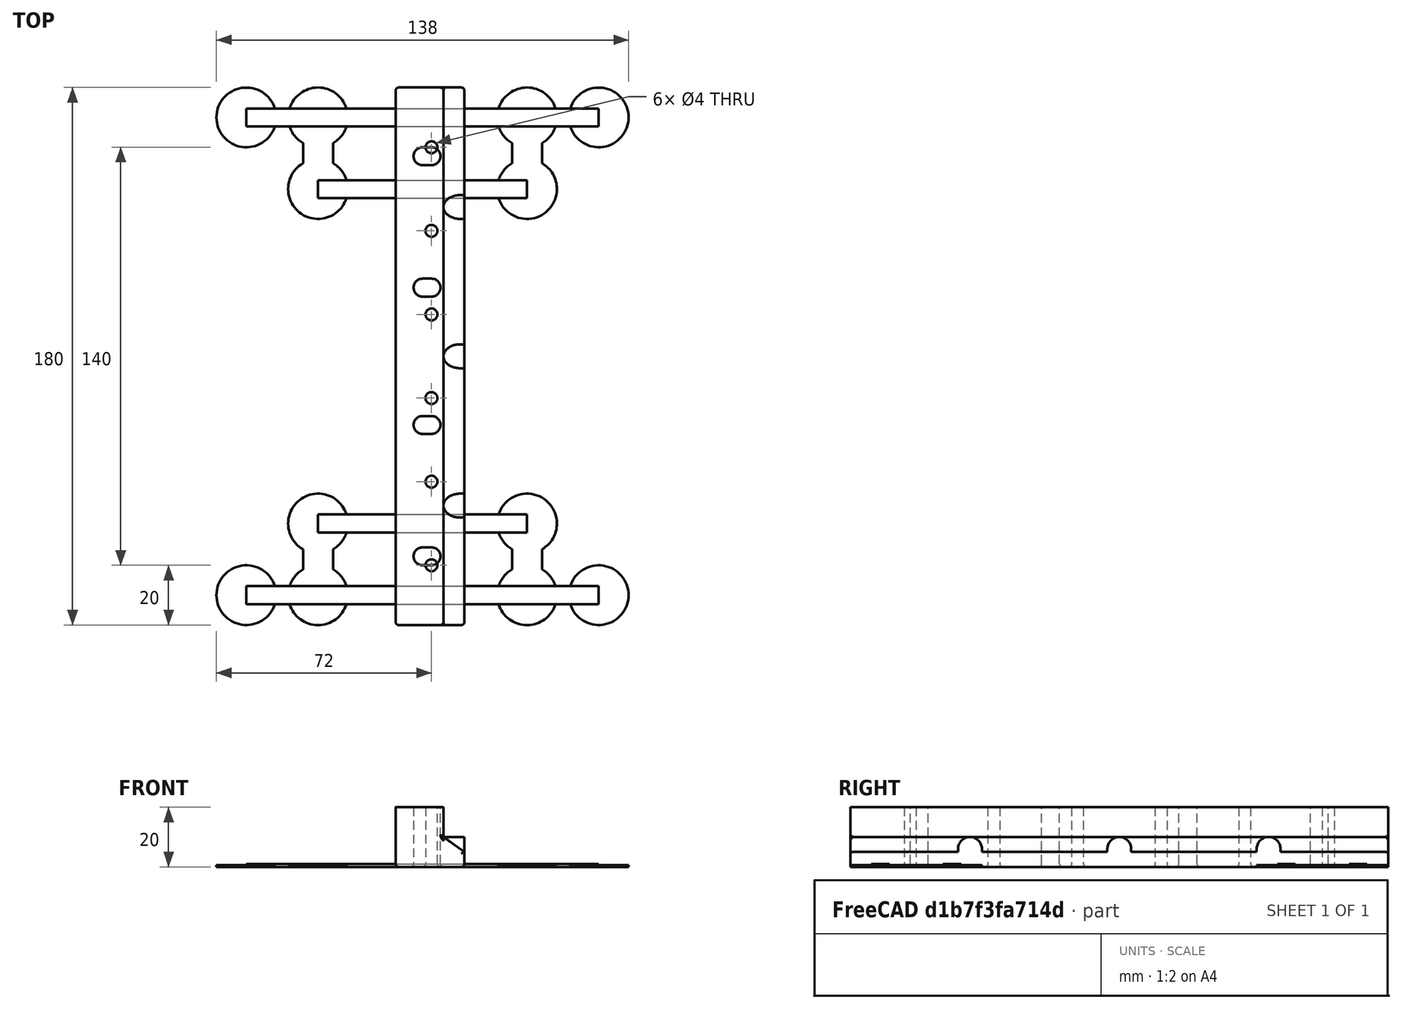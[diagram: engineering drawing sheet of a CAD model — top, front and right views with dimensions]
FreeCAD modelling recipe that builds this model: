
FCSTD DOCUMENT  (FreeCAD 0.21R33771 (Git))
Label: Battery_Bracket
License: All rights reserved
LicenseURL: https://en.wikipedia.org/wiki/All_rights_reserved
objects: Part::Cylinder×32, Part::Box×22, Part::MultiFuse×13, Part::Cut×10, App::Part×3, Part::Chamfer×2, Part::Fillet×2
note: 81 computed .brp shape members not serialized (recipe doc carries the construction recipe); baked Part::Feature solids carry a one-line shape summary decoded from their .brp

FEATURE [Part::Box] Box  label="Cube"
  AttacherType = Attacher::AttachEngine3D
  Height = 10
  Length = 23
  Placement = pos=(-4,0,5) rot=(0,0,1;0rad)
  Width = 180
FEATURE [Part::Cylinder] Cylinder
  Angle = 180
  AttacherType = Attacher::AttachEngine3D
  FirstAngle = 0
  Height = 7
  Placement = pos=(12,90,11) rot=(0.57735,0.57735,0.57735;2.0944rad)
  Radius = 4
  SecondAngle = 0
FEATURE [Part::Cylinder] Cylinder001
  Angle = 180
  AttacherType = Attacher::AttachEngine3D
  FirstAngle = 0
  Height = 7
  Placement = pos=(12,140,11) rot=(0.57735,0.57735,0.57735;2.0944rad)
  Radius = 4
  SecondAngle = 0
FEATURE [Part::Cylinder] Cylinder002
  Angle = 180
  AttacherType = Attacher::AttachEngine3D
  FirstAngle = 0
  Height = 7
  Placement = pos=(12,40,11) rot=(0.57735,0.57735,0.57735;2.0944rad)
  Radius = 4
  SecondAngle = 0
FEATURE [Part::Box] Box001  label="Cube001"
  AttacherType = Attacher::AttachEngine3D
  Height = 1
  Length = 7
  Placement = pos=(12,86,10) rot=(0,0,1;0rad)
  Width = 8
FEATURE [Part::Box] Box002  label="Cube002"
  AttacherType = Attacher::AttachEngine3D
  Height = 1
  Length = 7
  Placement = pos=(12,136,10) rot=(0,0,1;0rad)
  Width = 8
FEATURE [Part::Box] Box003  label="Cube003"
  AttacherType = Attacher::AttachEngine3D
  Height = 1
  Length = 7
  Placement = pos=(12,36,10) rot=(0,0,1;0rad)
  Width = 8
FEATURE [Part::MultiFuse] Fusion  label="Fusion000"
  Shapes = -> [Box002,Cylinder001]
FEATURE [Part::MultiFuse] Fusion001
  Shapes = -> [Cylinder,Box001]
FEATURE [Part::MultiFuse] Fusion002
  Shapes = -> [Cylinder002,Box003]
FEATURE [Part::Cylinder] Cylinder003
  Angle = 360
  AttacherType = Attacher::AttachEngine3D
  FirstAngle = 0
  Height = 20
  Placement = pos=(8,23,5) rot=(0,0,1;0rad)
  Radius = 3
  SecondAngle = 0
FEATURE [Part::Cylinder] Cylinder004
  Angle = 360
  AttacherType = Attacher::AttachEngine3D
  FirstAngle = 0
  Height = 20
  Placement = pos=(8,157,5) rot=(0,0,1;0rad)
  Radius = 3
  SecondAngle = 0
FEATURE [Part::Chamfer] Chamfer
  Base = -> Box
  Edges = 1 edges: [Edge6 r1=5 r2=7]
FEATURE [Part::Box] Box005  label="Cube005"
  AttacherType = Attacher::AttachEngine3D
  Height = 10
  Length = 16
  Placement = pos=(-4,0,15) rot=(0,0,1;0rad)
  Width = 180
FEATURE [Part::Box] Box008  label="Cube008"
  AttacherType = Attacher::AttachEngine3D
  Height = 10
  Length = 23
  Placement = pos=(-4,0,5) rot=(0,0,1;0rad)
  Width = 180
FEATURE [Part::Box] Box009  label="Cube009"
  AttacherType = Attacher::AttachEngine3D
  Height = 1
  Length = 7
  Placement = pos=(12,86,10) rot=(0,0,1;0rad)
  Width = 8
FEATURE [Part::Box] Box010  label="Cube010"
  AttacherType = Attacher::AttachEngine3D
  Height = 1
  Length = 7
  Placement = pos=(12,136,10) rot=(0,0,1;0rad)
  Width = 8
FEATURE [Part::Box] Box011  label="Cube011"
  AttacherType = Attacher::AttachEngine3D
  Height = 1
  Length = 7
  Placement = pos=(12,36,10) rot=(0,0,1;0rad)
  Width = 8
FEATURE [Part::Box] Box012  label="Cube012"
  AttacherType = Attacher::AttachEngine3D
  Height = 10
  Length = 16
  Placement = pos=(-4,0,15) rot=(0,0,1;0rad)
  Width = 180
FEATURE [Part::Chamfer] Chamfer001
  Base = -> Box008
  Edges = 1 edges: [Edge6 r1=5 r2=7]
FEATURE [Part::Cylinder] Cylinder005
  Angle = 180
  AttacherType = Attacher::AttachEngine3D
  FirstAngle = 0
  Height = 7
  Placement = pos=(12,90,11) rot=(0.57735,0.57735,0.57735;2.0944rad)
  Radius = 4
  SecondAngle = 0
FEATURE [Part::Cylinder] Cylinder006
  Angle = 180
  AttacherType = Attacher::AttachEngine3D
  FirstAngle = 0
  Height = 7
  Placement = pos=(12,140,11) rot=(0.57735,0.57735,0.57735;2.0944rad)
  Radius = 4
  SecondAngle = 0
FEATURE [Part::Cylinder] Cylinder007
  Angle = 180
  AttacherType = Attacher::AttachEngine3D
  FirstAngle = 0
  Height = 7
  Placement = pos=(12,40,11) rot=(0.57735,0.57735,0.57735;2.0944rad)
  Radius = 4
  SecondAngle = 0
FEATURE [Part::Cylinder] Cylinder009
  Angle = 360
  AttacherType = Attacher::AttachEngine3D
  FirstAngle = 0
  Height = 20
  Placement = pos=(8,160,5) rot=(0,0,1;0rad)
  Radius = 2
  SecondAngle = 0
FEATURE [Part::MultiFuse] Fusion004
  Shapes = -> [Box010,Cylinder006]
FEATURE [Part::MultiFuse] Fusion005
  Shapes = -> [Cylinder005,Box009]
FEATURE [Part::MultiFuse] Fusion006
  Shapes = -> [Cylinder007,Box011]
FEATURE [Part::Cylinder] Cylinder010 .. Cylinder014  x5 (patterned run collapsed; names and placements below)
  Angle = 360
  AttacherType = Attacher::AttachEngine3D
  FirstAngle = 0
  Height = 20
  Radius = 2
  SecondAngle = 0
  placements: 5 in arithmetic series — first pos=(8,132,5) rot=(0,0,1;0rad), step (0,-28,0), last pos=(8,20,5) rot=(0,0,1;0rad)
FEATURE [Part::MultiFuse] Fusion009
  Shapes = -> [Chamfer001,Box012,Fusion006,Fusion005,Fusion004]
FEATURE [Part::Cylinder] Cylinder015
  Angle = 360
  AttacherType = Attacher::AttachEngine3D
  FirstAngle = 0
  Height = 20
  Placement = pos=(5,157,5) rot=(0,0,1;0rad)
  Radius = 3
  SecondAngle = 0
FEATURE [Part::Cylinder] Cylinder016
  Angle = 360
  AttacherType = Attacher::AttachEngine3D
  FirstAngle = 0
  Height = 20
  Placement = pos=(5,23,5) rot=(0,0,1;0rad)
  Radius = 3
  SecondAngle = 0
FEATURE [Part::Box] Box013  label="Cube013"
  AttacherType = Attacher::AttachEngine3D
  Height = 20
  Length = 3
  Placement = pos=(5,20,5) rot=(0,0,1;0rad)
  Width = 6
FEATURE [Part::Box] Box014  label="Cube014"
  AttacherType = Attacher::AttachEngine3D
  Height = 20
  Length = 3
  Placement = pos=(5,154,5) rot=(0,0,1;0rad)
  Width = 6
FEATURE [Part::MultiFuse] Fusion010
  Shapes = -> [Box014,Cylinder015,Cylinder004]
FEATURE [Part::MultiFuse] Fusion011
  Shapes = -> [Cylinder003,Cylinder016,Box013]
FEATURE [Part::Cylinder] Cylinder017
  Angle = 360
  AttacherType = Attacher::AttachEngine3D
  FirstAngle = 0
  Height = 0.6
  Placement = pos=(-54,10,5) rot=(0,0,1;0rad)
  Radius = 10
  SecondAngle = 0
FEATURE [Part::Cylinder] Cylinder018
  Angle = 360
  AttacherType = Attacher::AttachEngine3D
  FirstAngle = 0
  Height = 0.6
  Placement = pos=(64,10,5) rot=(0,0,1;0rad)
  Radius = 10
  SecondAngle = 0
FEATURE [Part::Cylinder] Cylinder019
  Angle = 360
  AttacherType = Attacher::AttachEngine3D
  FirstAngle = 0
  Height = 0.6
  Placement = pos=(-54,170,5) rot=(0,0,1;0rad)
  Radius = 10
  SecondAngle = 0
FEATURE [Part::Cylinder] Cylinder020
  Angle = 360
  AttacherType = Attacher::AttachEngine3D
  FirstAngle = 0
  Height = 0.6
  Placement = pos=(40,146,5) rot=(0,0,1;0rad)
  Radius = 10
  SecondAngle = 0
FEATURE [Part::Box] Box015  label="Cube015"
  AttacherType = Attacher::AttachEngine3D
  Height = 1
  Length = 70
  Placement = pos=(-30,31,5) rot=(0,0,1;0rad)
  Width = 6
FEATURE [Part::Box] Box016  label="Cube016"
  AttacherType = Attacher::AttachEngine3D
  Height = 1
  Length = 70
  Placement = pos=(-30,143,5) rot=(0,0,1;0rad)
  Width = 6
FEATURE [Part::Box] Box017  label="Cube017"
  AttacherType = Attacher::AttachEngine3D
  Height = 20
  Length = 3
  Placement = pos=(5,20,5) rot=(0,0,1;0rad)
  Width = 6
FEATURE [Part::Cylinder] Cylinder021
  Angle = 360
  AttacherType = Attacher::AttachEngine3D
  FirstAngle = 0
  Height = 20
  Placement = pos=(8,23,5) rot=(0,0,1;0rad)
  Radius = 3
  SecondAngle = 0
FEATURE [Part::Cylinder] Cylinder022
  Angle = 360
  AttacherType = Attacher::AttachEngine3D
  FirstAngle = 0
  Height = 20
  Placement = pos=(5,23,5) rot=(0,0,1;0rad)
  Radius = 3
  SecondAngle = 0
FEATURE [Part::MultiFuse] Fusion013
  Placement = pos=(0,90,0) rot=(0,0,1;0rad)
  Shapes = -> [Cylinder021,Cylinder022,Box017]
FEATURE [Part::Box] Box018  label="Cube018"
  AttacherType = Attacher::AttachEngine3D
  Height = 20
  Length = 3
  Placement = pos=(5,20,5) rot=(0,0,1;0rad)
  Width = 6
FEATURE [Part::Cylinder] Cylinder023
  Angle = 360
  AttacherType = Attacher::AttachEngine3D
  FirstAngle = 0
  Height = 20
  Placement = pos=(8,23,5) rot=(0,0,1;0rad)
  Radius = 3
  SecondAngle = 0
FEATURE [Part::Cylinder] Cylinder024
  Angle = 360
  AttacherType = Attacher::AttachEngine3D
  FirstAngle = 0
  Height = 20
  Placement = pos=(5,23,5) rot=(0,0,1;0rad)
  Radius = 3
  SecondAngle = 0
FEATURE [Part::MultiFuse] Fusion014
  Placement = pos=(0,44,0) rot=(0,0,1;0rad)
  Shapes = -> [Cylinder023,Cylinder024,Box018]
FEATURE [Part::MultiFuse] Fusion016
  Shapes = -> [Box005,Fusion001,Fusion002,Fusion,Chamfer]
FEATURE [Part::Cut] Cut006
  Base = -> Fusion016
  Tool = -> Fusion010
FEATURE [Part::Cut] Cut007
  Base = -> Cut006
  Tool = -> Fusion014
FEATURE [Part::Cut] Cut008
  Base = -> Cut007
  Tool = -> Fusion013
FEATURE [Part::Cut] Cut009
  Base = -> Cut008
  Tool = -> Fusion011
FEATURE [Part::Fillet] Fillet001
  Base = -> Cut009
  Edges = 34 edges r=1: [Edge1,Edge3,Edge6,Edge31,Edge32,Edge33,Edge34,Edge35,Edge36,Edge37,Edge42,Edge45,Edge47,Edge49,Edge51,Edge52,Edge56,Edge57,Edge59,Edge61,Edge62,Edge66,Edge67,Edge69,Edge71,Edge72,Edge76,Edge77,Edge79,Edge81,Edge82,Edge83,Edge84,Edge85]
FEATURE [App::Part] Part  label="Front"
  Group = -> [Cut007,Cut008,Fusion016,Cut006,Box,Fusion001,Fusion002,Cylinder,Cylinder001,Cylinder002,Box001,Box002,Box003,Fusion,Cylinder003,Cylinder004,Chamfer,Box005,Cylinder015,Cylinder016,Box013,Box014,Fusion010,Fusion011,Box017,Cylinder021,Cylinder022,Fusion013,Box018,Cylinder023,Cylinder024,Fusion014,Cut009,Fillet001]
  Origin = -> Origin
  Placement = pos=(0,180,0) rot=(0,0,1;3.14159rad)
FEATURE [Part::Cut] Cut
  Base = -> Fusion009
  Tool = -> Cylinder009
FEATURE [Part::Cut] Cut010
  Base = -> Cut
  Tool = -> Cylinder010
FEATURE [Part::Cut] Cut011
  Base = -> Cut010
  Tool = -> Cylinder011
FEATURE [Part::Cut] Cut012
  Base = -> Cut011
  Tool = -> Cylinder012
FEATURE [Part::Cut] Cut013
  Base = -> Cut012
  Tool = -> Cylinder013
FEATURE [Part::Cut] Cut014
  Base = -> Cut013
  Tool = -> Cylinder014
FEATURE [Part::Fillet] Fillet
  Base = -> Cut014
  Edges = 20 edges r=1: [Edge1,Edge3,Edge6,Edge17,Edge18,Edge19,Edge20,Edge21,Edge22,Edge23,Edge29,Edge31,Edge33,Edge35,Edge37,Edge39,Edge40,Edge41,Edge42,Edge43]
FEATURE [App::Part] Part001  label="Rear"
  Group = -> [Cut013,Cut011,Cut010,Cut012,Box008,Box009,Box010,Box011,Box012,Chamfer001,Cylinder005,Cylinder006,Cylinder007,Cylinder009,Fusion004,Fusion005,Fusion006,Cylinder010,Cylinder011,Cylinder012,Cylinder013,Cylinder014,Fusion009,Cut,Cut014,Fillet]
  Origin = -> Origin001
  Placement = pos=(10,0,0) rot=(0,0,1;0rad)
FEATURE [Part::Cylinder] Cylinder025
  Angle = 360
  AttacherType = Attacher::AttachEngine3D
  FirstAngle = 0
  Height = 0.6
  Placement = pos=(40,34,5) rot=(0,0,1;0rad)
  Radius = 10
  SecondAngle = 0
FEATURE [Part::Cylinder] Cylinder026
  Angle = 360
  AttacherType = Attacher::AttachEngine3D
  FirstAngle = 0
  Height = 0.6
  Placement = pos=(-30,34,5) rot=(0,0,1;0rad)
  Radius = 10
  SecondAngle = 0
FEATURE [Part::Cylinder] Cylinder027
  Angle = 360
  AttacherType = Attacher::AttachEngine3D
  FirstAngle = 0
  Height = 0.6
  Placement = pos=(-30,146,5) rot=(0,0,1;0rad)
  Radius = 10
  SecondAngle = 0
FEATURE [Part::Cylinder] Cylinder028
  Angle = 360
  AttacherType = Attacher::AttachEngine3D
  FirstAngle = 0
  Height = 0.6
  Placement = pos=(64,170,5) rot=(0,0,1;0rad)
  Radius = 10
  SecondAngle = 0
FEATURE [Part::Cylinder] Cylinder029
  Angle = 360
  AttacherType = Attacher::AttachEngine3D
  FirstAngle = 0
  Height = 0.6
  Placement = pos=(40,170,5) rot=(0,0,1;0rad)
  Radius = 10
  SecondAngle = 0
FEATURE [Part::Cylinder] Cylinder030
  Angle = 360
  AttacherType = Attacher::AttachEngine3D
  FirstAngle = 0
  Height = 0.6
  Placement = pos=(-30,170,5) rot=(0,0,1;0rad)
  Radius = 10
  SecondAngle = 0
FEATURE [Part::Cylinder] Cylinder031
  Angle = 360
  AttacherType = Attacher::AttachEngine3D
  FirstAngle = 0
  Height = 0.6
  Placement = pos=(-30,10,5) rot=(0,0,1;0rad)
  Radius = 10
  SecondAngle = 0
FEATURE [Part::Cylinder] Cylinder032
  Angle = 360
  AttacherType = Attacher::AttachEngine3D
  FirstAngle = 0
  Height = 0.6
  Placement = pos=(40,10,5) rot=(0,0,1;0rad)
  Radius = 10
  SecondAngle = 0
FEATURE [Part::Box] Box019  label="Cube019"
  AttacherType = Attacher::AttachEngine3D
  Height = 1
  Length = 118
  Placement = pos=(-54,7,5) rot=(0,0,1;0rad)
  Width = 6
FEATURE [Part::Box] Box020  label="Cube020"
  AttacherType = Attacher::AttachEngine3D
  Height = 1
  Length = 118
  Placement = pos=(-54,167,5) rot=(0,0,1;0rad)
  Width = 6
FEATURE [Part::Box] Box021  label="Cube021"
  AttacherType = Attacher::AttachEngine3D
  Height = 0.6
  Length = 10
  Placement = pos=(-35,17,5) rot=(0,0,1;0rad)
  Width = 10
FEATURE [Part::Box] Box022  label="Cube022"
  AttacherType = Attacher::AttachEngine3D
  Height = 0.6
  Length = 10
  Placement = pos=(35,17,5) rot=(0,0,1;0rad)
  Width = 10
FEATURE [Part::Box] Box023  label="Cube023"
  AttacherType = Attacher::AttachEngine3D
  Height = 0.6
  Length = 10
  Placement = pos=(35,153,5) rot=(0,0,1;0rad)
  Width = 10
FEATURE [Part::Box] Box024  label="Cube024"
  AttacherType = Attacher::AttachEngine3D
  Height = 0.6
  Length = 10
  Placement = pos=(-35,153,5) rot=(0,0,1;0rad)
  Width = 10
FEATURE [Part::MultiFuse] Fusion017
  Shapes = -> [Cylinder017,Cylinder018,Cylinder019,Cylinder020,Box015,Box016,Cylinder025,Cylinder026,Cylinder027,Cylinder028,Cylinder029,Cylinder030,Cylinder031,Cylinder032,Box019,Box020,Box021,Box022,Box023,Box024]
FEATURE [App::Part] Part002  label="PrintSupport"
  Group = -> [Box022,Box021,Cylinder031,Cylinder017,Cylinder018,Cylinder019,Cylinder020,Box015,Box016,Cylinder032,Cylinder025,Box020,Cylinder026,Cylinder027,Cylinder028,Box019,Cylinder030,Cylinder029,Box023,Box024,Fusion017]
  Origin = -> Origin002
